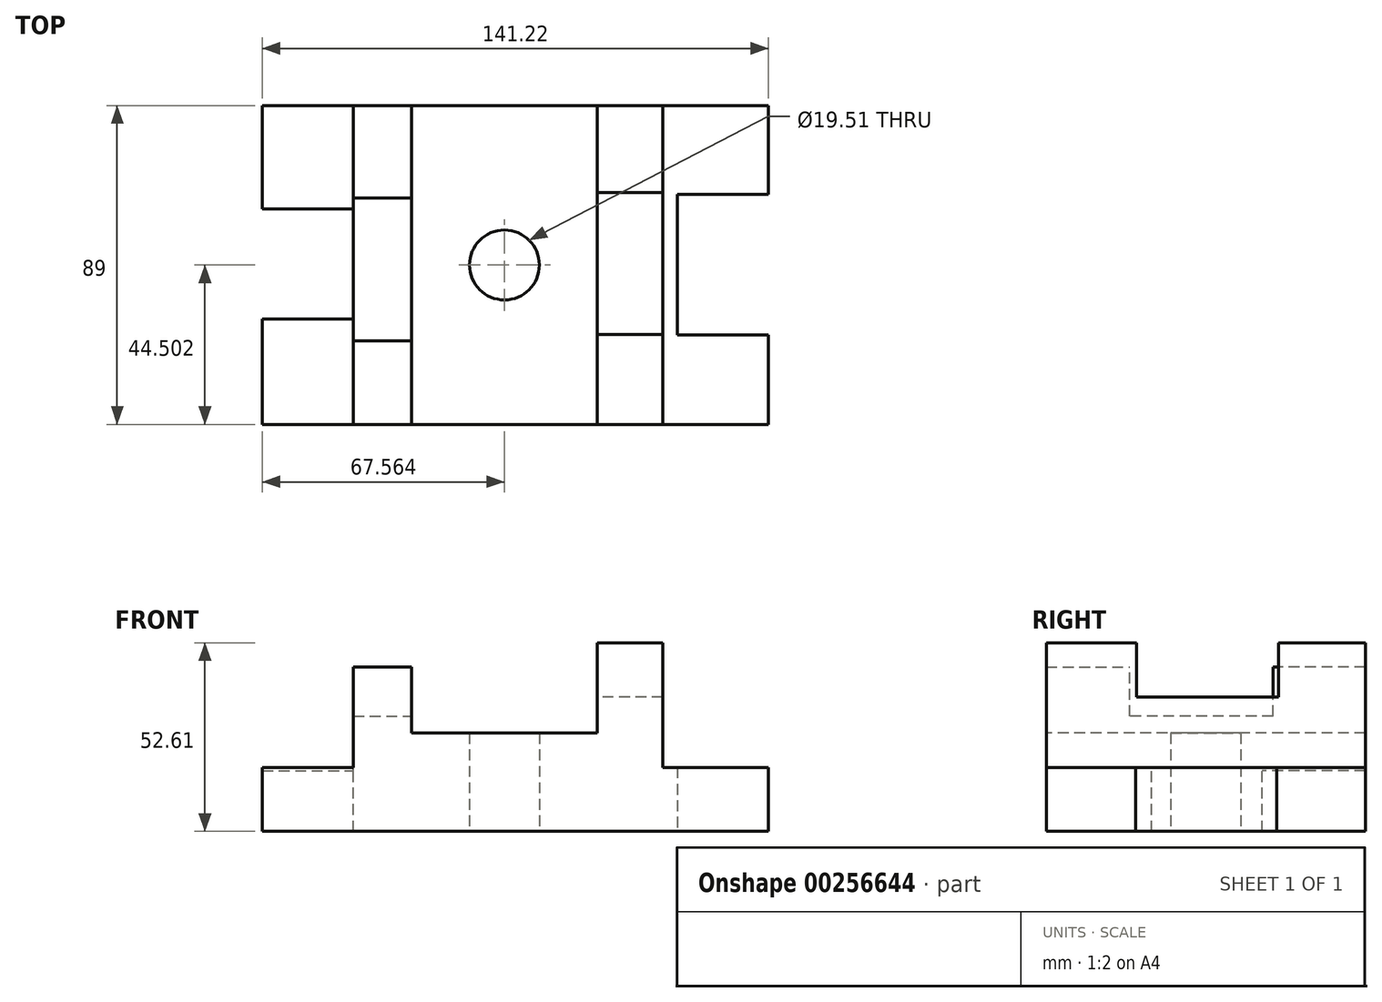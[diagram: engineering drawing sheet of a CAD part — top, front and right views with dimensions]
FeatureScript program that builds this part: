
annotation { "Feature Type Name" : "Feature", "Feature Type Description" : "" }
export const myFeature = defineFeature(function(context is Context, id is Id, definition is map)
    precondition{}
    {
        {
            var Q0;
            Q0=qCreatedBy(makeId("Top.planeOp"),FACE);
            var sketch = newSketch(context, id + "F0", { "sketchPlane" : qUnion([Q0])});
            skLineSegment(sketch, "E0.bottom", {"start": v(-24.38, 52.27) * mm, "end": v(27.43, 52.27) * mm});
            skLineSegment(sketch, "E0.top", {"start": v(-24.38, -36.73) * mm, "end": v(27.43, -36.73) * mm});
            skLineSegment(sketch, "E0.left", {"start": v(-24.38, 52.27) * mm, "end": v(-24.38, -36.73) * mm});
            skLineSegment(sketch, "E0.right", {"start": v(27.43, 52.27) * mm, "end": v(27.43, -36.73) * mm});
            skCircle(sketch, "E1", {"center": v(1.52, 7.77) * mm, "radius": 9.75 * mm});
            skPoint(sketch, "E1.centerSnap0", {"position": v(-24.38, 7.77) * mm});
            skPoint(sketch, "E1.centerSnap1", {"position": v(1.52, 52.27) * mm});
            skSolve(sketch);
        }
        {
            var Q0;
            Q0 = qSketchRegion(id + "F0", true);
            extrude(context, id + "F1", {"entities" : qUnion([Q0]), "depth" : 27.43 * mm});
        }
        {
            var Q0;
            Q0=makeQuery(id+"F1.opExtrude","SWEPT_FACE",FACE,{"disambiguationData":[OSD([sQuery(id+"F0.wireOp",EDGE,"E0.right")])]});
            var sketch = newSketch(context, id + "F2", { "sketchPlane" : qUnion([Q0])});
            skLineSegment(sketch, "E2.bottom", {"start": v(-36.73, 37.45) * mm, "end": v(52.27, 37.45) * mm});
            skLineSegment(sketch, "E2.top", {"start": v(-36.73, 0) * mm, "end": v(52.27, 0) * mm});
            skLineSegment(sketch, "E2.left", {"start": v(-36.73, 37.45) * mm, "end": v(-36.73, 0) * mm});
            skLineSegment(sketch, "E2.right", {"start": v(52.27, 37.45) * mm, "end": v(52.27, 0) * mm});
            skLineSegment(sketch, "E3.bottom", {"start": v(-36.73, 37.45) * mm, "end": v(-11.58, 37.45) * mm});
            skLineSegment(sketch, "E3.top", {"start": v(-36.73, 52.6) * mm, "end": v(-11.58, 52.6) * mm});
            skLineSegment(sketch, "E3.left", {"start": v(-36.73, 37.45) * mm, "end": v(-36.73, 52.6) * mm});
            skLineSegment(sketch, "E3.right", {"start": v(-11.58, 37.45) * mm, "end": v(-11.58, 52.6) * mm});
            skLineSegment(sketch, "E4.bottom", {"start": v(52.27, 37.45) * mm, "end": v(28.04, 37.45) * mm});
            skLineSegment(sketch, "E4.top", {"start": v(52.27, 52.6) * mm, "end": v(28.04, 52.6) * mm});
            skLineSegment(sketch, "E4.left", {"start": v(52.27, 37.45) * mm, "end": v(52.27, 52.6) * mm});
            skLineSegment(sketch, "E4.right", {"start": v(28.04, 37.45) * mm, "end": v(28.04, 52.6) * mm});
            skSolve(sketch);
        }
        {
            var Q0;
            Q0 = qSketchRegion(id + "F2", true);
            extrude(context, id + "F3", {"entities" : qUnion([Q0]), "operationType" : NewBodyOperationType.ADD, "depth" : 18.29 * mm});
        }
        {
            var Q0;
            Q0=makeQuery(id+"F1.opExtrude","SWEPT_FACE",FACE,{"disambiguationData":[OSD([sQuery(id+"F0.wireOp",EDGE,"E0.left")])]});
            var sketch = newSketch(context, id + "F4", { "sketchPlane" : qUnion([Q0])});
            skLineSegment(sketch, "E5.bottom", {"start": v(-52.27, 32.16) * mm, "end": v(36.73, 32.16) * mm});
            skLineSegment(sketch, "E5.top", {"start": v(-52.27, 0) * mm, "end": v(36.73, 0) * mm});
            skLineSegment(sketch, "E5.left", {"start": v(-52.27, 32.16) * mm, "end": v(-52.27, 0) * mm});
            skLineSegment(sketch, "E5.right", {"start": v(36.73, 32.16) * mm, "end": v(36.73, 0) * mm});
            skLineSegment(sketch, "E6.bottom", {"start": v(-52.27, 32.16) * mm, "end": v(-26.52, 32.16) * mm});
            skLineSegment(sketch, "E6.top", {"start": v(-52.27, 45.87) * mm, "end": v(-26.52, 45.87) * mm});
            skLineSegment(sketch, "E6.left", {"start": v(-52.27, 32.16) * mm, "end": v(-52.27, 45.87) * mm});
            skLineSegment(sketch, "E6.right", {"start": v(-26.52, 32.16) * mm, "end": v(-26.52, 45.87) * mm});
            skLineSegment(sketch, "E7.bottom", {"start": v(36.73, 32.16) * mm, "end": v(13.41, 32.16) * mm});
            skLineSegment(sketch, "E7.top", {"start": v(36.73, 45.87) * mm, "end": v(13.41, 45.87) * mm});
            skLineSegment(sketch, "E7.left", {"start": v(36.73, 32.16) * mm, "end": v(36.73, 45.87) * mm});
            skLineSegment(sketch, "E7.right", {"start": v(13.41, 32.16) * mm, "end": v(13.41, 45.87) * mm});
            skSolve(sketch);
        }
        {
            var Q0;
            Q0 = qSketchRegion(id + "F4", true);
            extrude(context, id + "F5", {"entities" : qUnion([Q0]), "operationType" : NewBodyOperationType.ADD, "depth" : 16.26 * mm});
        }
        {
            var Q0;
            Q0=makeQuery(id+"F3.opExtrude","CAP_FACE",FACE,{"disambiguationData":[OSD([sQuery(id+"F2.wireOp",EDGE,"E2.bottom"),sQuery(id+"F2.wireOp",EDGE,"E2.top"),sQuery(id+"F2.wireOp",EDGE,"E2.left"),sQuery(id+"F2.wireOp",EDGE,"E2.right"),sQuery(id+"F2.wireOp",EDGE,"E3.top"),sQuery(id+"F2.wireOp",EDGE,"E3.left"),sQuery(id+"F2.wireOp",EDGE,"E3.right"),sQuery(id+"F2.wireOp",EDGE,"E4.top"),sQuery(id+"F2.wireOp",EDGE,"E4.left"),sQuery(id+"F2.wireOp",EDGE,"E4.right")])],"isStart":false});
            var sketch = newSketch(context, id + "F6", { "sketchPlane" : qUnion([Q0])});
            skLineSegment(sketch, "E8.bottom", {"start": v(-36.73, 17.83) * mm, "end": v(52.27, 17.83) * mm});
            skLineSegment(sketch, "E8.top", {"start": v(-36.73, 0) * mm, "end": v(52.27, 0) * mm});
            skLineSegment(sketch, "E8.left", {"start": v(-36.73, 17.83) * mm, "end": v(-36.73, 0) * mm});
            skLineSegment(sketch, "E8.right", {"start": v(52.27, 17.83) * mm, "end": v(52.27, 0) * mm});
            skSolve(sketch);
        }
        {
            var Q0;
            Q0 = qSketchRegion(id + "F6", true);
            extrude(context, id + "F7", {"entities" : qUnion([Q0]), "operationType" : NewBodyOperationType.ADD, "depth" : 4.06 * mm});
        }
        {
            var Q0;
            Q0=makeQuery(id+"F7.opExtrude","CAP_FACE",FACE,{"disambiguationData":[OSD([sQuery(id+"F6.wireOp",EDGE,"E8.bottom"),sQuery(id+"F6.wireOp",EDGE,"E8.top"),sQuery(id+"F6.wireOp",EDGE,"E8.left"),sQuery(id+"F6.wireOp",EDGE,"E8.right")])],"isStart":false});
            var sketch = newSketch(context, id + "F8", { "sketchPlane" : qUnion([Q0])});
            skLineSegment(sketch, "E9.bottom", {"start": v(-36.73, 17.83) * mm, "end": v(-11.78, 17.83) * mm});
            skLineSegment(sketch, "E9.top", {"start": v(-36.73, 0) * mm, "end": v(-11.78, 0) * mm});
            skLineSegment(sketch, "E9.left", {"start": v(-36.73, 17.83) * mm, "end": v(-36.73, 0) * mm});
            skLineSegment(sketch, "E9.right", {"start": v(-11.78, 17.83) * mm, "end": v(-11.78, 0) * mm});
            skLineSegment(sketch, "E10.bottom", {"start": v(52.27, 17.83) * mm, "end": v(27.54, 17.83) * mm});
            skLineSegment(sketch, "E10.top", {"start": v(52.27, 0) * mm, "end": v(27.54, 0) * mm});
            skLineSegment(sketch, "E10.left", {"start": v(52.27, 17.83) * mm, "end": v(52.27, 0) * mm});
            skLineSegment(sketch, "E10.right", {"start": v(27.54, 17.83) * mm, "end": v(27.54, 0) * mm});
            skSolve(sketch);
        }
        {
            var Q0;
            Q0 = qSketchRegion(id + "F8", true);
            extrude(context, id + "F9", {"entities" : qUnion([Q0]), "operationType" : NewBodyOperationType.ADD, "depth" : 25.4 * mm});
        }
        {
            var Q0;
            Q0=makeQuery(id+"F5.opExtrude","CAP_FACE",FACE,{"disambiguationData":[OSD([sQuery(id+"F4.wireOp",EDGE,"E5.bottom"),sQuery(id+"F4.wireOp",EDGE,"E5.top"),sQuery(id+"F4.wireOp",EDGE,"E5.left"),sQuery(id+"F4.wireOp",EDGE,"E5.right"),sQuery(id+"F4.wireOp",EDGE,"E6.top"),sQuery(id+"F4.wireOp",EDGE,"E6.left"),sQuery(id+"F4.wireOp",EDGE,"E6.right"),sQuery(id+"F4.wireOp",EDGE,"E7.top"),sQuery(id+"F4.wireOp",EDGE,"E7.left"),sQuery(id+"F4.wireOp",EDGE,"E7.right")])],"isStart":false});
            var sketch = newSketch(context, id + "F10", { "sketchPlane" : qUnion([Q0])});
            skLineSegment(sketch, "E11.bottom", {"start": v(-52.27, 0) * mm, "end": v(-23.47, 0) * mm});
            skLineSegment(sketch, "E11.top", {"start": v(-52.27, 16.92) * mm, "end": v(-23.47, 16.92) * mm});
            skLineSegment(sketch, "E11.left", {"start": v(-52.27, 0) * mm, "end": v(-52.27, 16.92) * mm});
            skLineSegment(sketch, "E11.right", {"start": v(-23.47, 0) * mm, "end": v(-23.47, 16.92) * mm});
            skLineSegment(sketch, "E12.bottom", {"start": v(36.73, 0) * mm, "end": v(7.32, 0) * mm});
            skLineSegment(sketch, "E12.top", {"start": v(36.73, 17.83) * mm, "end": v(7.32, 17.83) * mm});
            skLineSegment(sketch, "E12.left", {"start": v(36.73, 0) * mm, "end": v(36.73, 17.83) * mm});
            skLineSegment(sketch, "E12.right", {"start": v(7.32, 0) * mm, "end": v(7.32, 17.83) * mm});
            skSolve(sketch);
        }
        {
            var Q0;
            Q0 = qSketchRegion(id + "F10", true);
            extrude(context, id + "F11", {"entities" : qUnion([Q0]), "operationType" : NewBodyOperationType.ADD, "depth" : 25.4 * mm});
        }
    });
